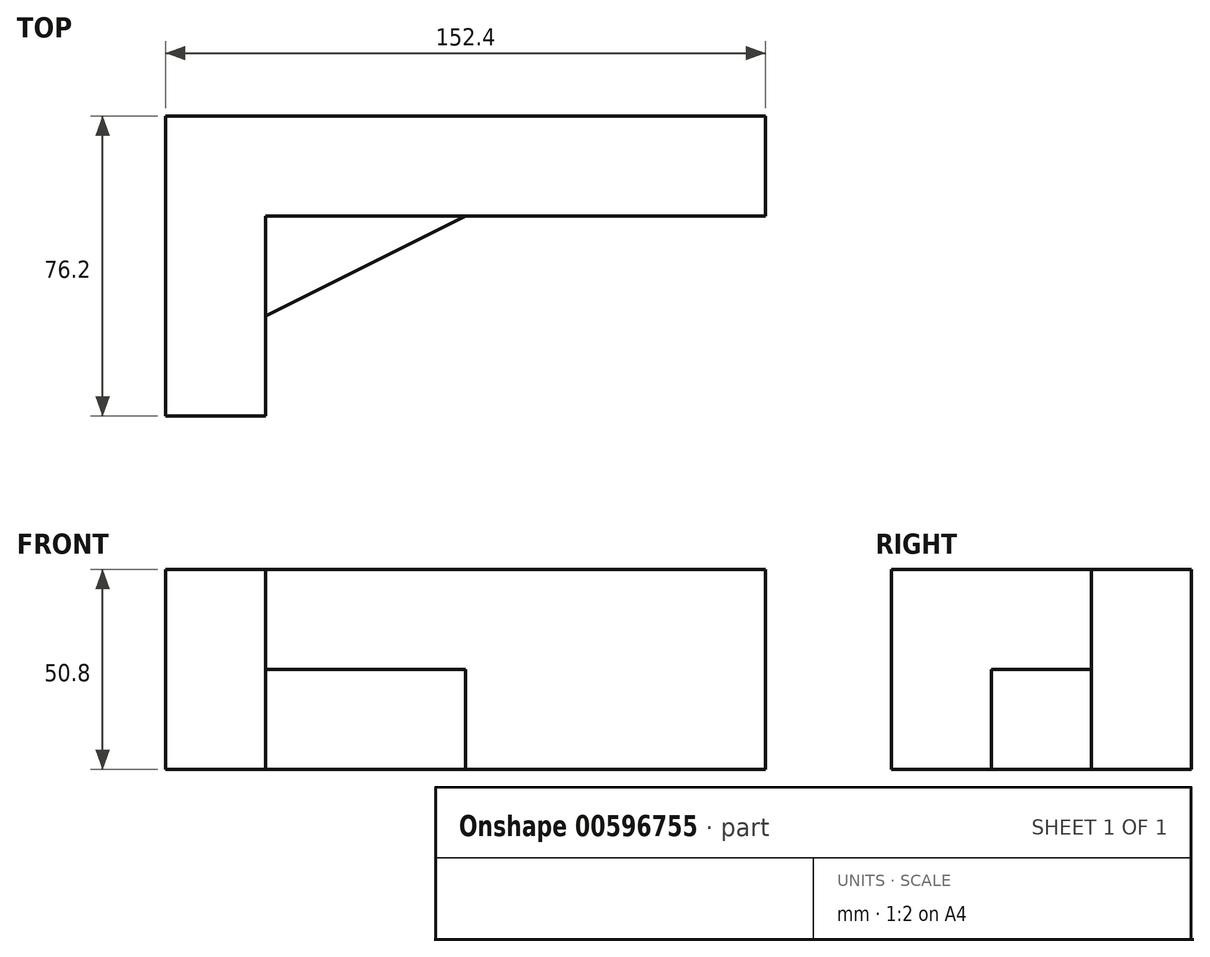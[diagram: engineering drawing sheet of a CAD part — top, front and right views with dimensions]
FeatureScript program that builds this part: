
annotation { "Feature Type Name" : "Feature", "Feature Type Description" : "" }
export const myFeature = defineFeature(function(context is Context, id is Id, definition is map)
    precondition{}
    {
        {
            var Q0;
            Q0=qCreatedBy(makeId("Top.planeOp"),FACE);
            var sketch = newSketch(context, id + "F0", { "sketchPlane" : qUnion([Q0])});
            skLineSegment(sketch, "E0", {"start": v(0, 60.6) * mm, "end": v(0, 136.8) * mm});
            skLineSegment(sketch, "E1", {"start": v(0, 136.8) * mm, "end": v(152.4, 136.8) * mm});
            skLineSegment(sketch, "E2", {"start": v(152.4, 136.8) * mm, "end": v(152.4, 111.4) * mm});
            skLineSegment(sketch, "E3", {"start": v(152.4, 111.4) * mm, "end": v(76.2, 111.4) * mm});
            skLineSegment(sketch, "E4", {"start": v(76.2, 111.4) * mm, "end": v(25.4, 111.4) * mm});
            skLineSegment(sketch, "E5", {"start": v(25.4, 111.4) * mm, "end": v(25.4, 86) * mm});
            skLineSegment(sketch, "E6", {"start": v(25.4, 86) * mm, "end": v(25.4, 60.6) * mm});
            skLineSegment(sketch, "E7", {"start": v(25.4, 60.6) * mm, "end": v(0, 60.6) * mm});
            skLineSegment(sketch, "E8", {"start": v(25.4, 86) * mm, "end": v(76.2, 111.4) * mm});
            skSolve(sketch);
        }
        {
            var Q0;
            Q0=makeQuery(id+"F0.imprint","IMPRINT",FACE,{"disambiguationData":[TD([[makeQuery(id+"F0.imprint","IMPRINT",EDGE,{"derivedFrom":sQuery(id+"F0.wireOp",EDGE,"E4")}),1.0]])]});
            var Q1;
            Q1=makeQuery(id+"F0.imprint","IMPRINT",FACE,{"disambiguationData":[TD([[makeQuery(id+"F0.imprint","IMPRINT",EDGE,{"derivedFrom":sQuery(id+"F0.wireOp",EDGE,"E0")}),-1.0]])]});
            extrude(context, id + "F1", {"entities" : qUnion([Q0, Q1]), "depth" : 50.8 * mm, "offsetDistance" : 25.4 * mm});
        }
        {
            var Q0;
            Q0=makeQuery(id+"F1.opExtrude","CAP_FACE",FACE,{"disambiguationData":[OSD([sQuery(id+"F0.wireOp",EDGE,"E0"),sQuery(id+"F0.wireOp",EDGE,"E1"),sQuery(id+"F0.wireOp",EDGE,"E2"),sQuery(id+"F0.wireOp",EDGE,"E3"),sQuery(id+"F0.wireOp",EDGE,"E6"),sQuery(id+"F0.wireOp",EDGE,"E7"),sQuery(id+"F0.wireOp",EDGE,"E8")])],"isStart":false});
            var sketch = newSketch(context, id + "F2", { "sketchPlane" : qUnion([Q0])});
            skLineSegment(sketch, "E9", {"start": v(25.4, 86) * mm, "end": v(25.4, 111.4) * mm});
            skLineSegment(sketch, "E10", {"start": v(25.4, 111.4) * mm, "end": v(76.2, 111.4) * mm});
            skSolve(sketch);
        }
        {
            var Q0;
            Q0 = qSketchRegion(id + "F2", true);
            var Q1;
            Q1=makeQuery(id+"F2.imprint","IMPRINT",FACE,{"disambiguationData":[TD([[makeQuery(id+"F2.imprint","IMPRINT",EDGE,{"derivedFrom":sQuery(id+"F2.wireOp",EDGE,"E9")}),-1.0]])]});
            extrude(context, id + "F3", {"entities" : qUnion([Q0, Q1]), "operationType" : NewBodyOperationType.REMOVE, "oppositeDirection" : true, "depth" : 25.4 * mm, "offsetDistance" : 25.4 * mm});
        }
    });
